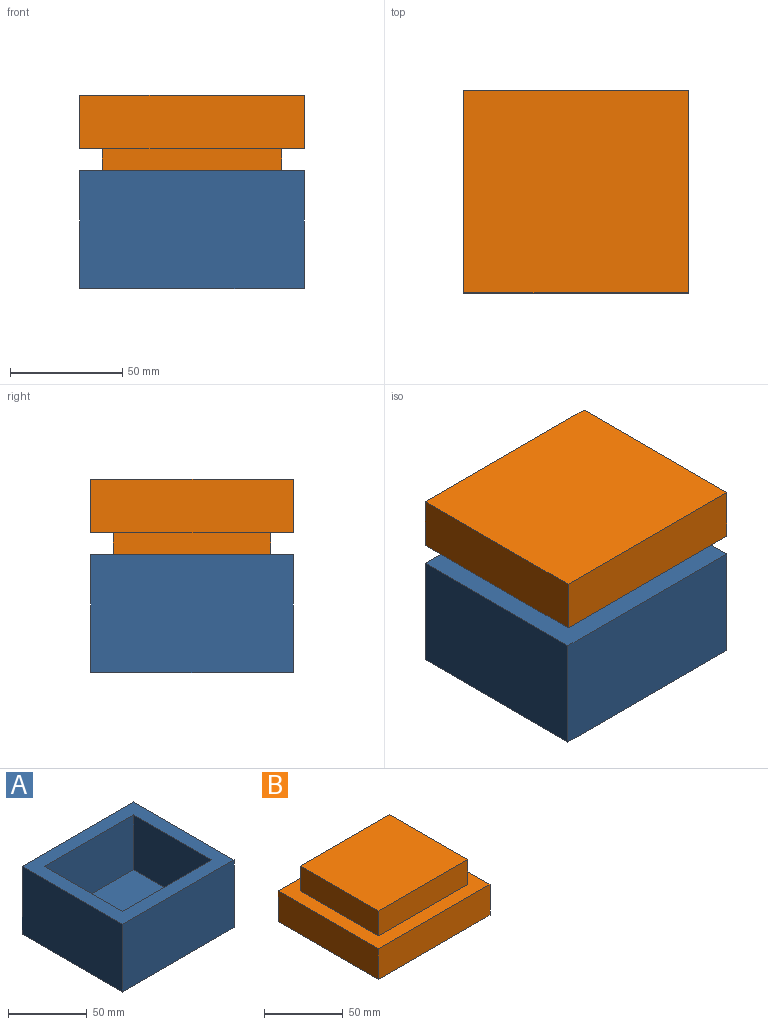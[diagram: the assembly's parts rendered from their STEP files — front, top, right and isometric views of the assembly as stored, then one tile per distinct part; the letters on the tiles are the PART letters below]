
ASSEMBLY  parts=2 mates=1
PART A: 11 faces, bbox 100x90x52.5 mm
  f0: plane 100x90mm, normal (0,0,1), area 3400mm2, adj f1,f2,f3,f4,f6,f7,f8,f9
  f1: plane 100x52.5mm, normal (0,1,0), area 5250mm2, adj f0,f2,f4,f5
  f2: plane 90x52.5mm, normal (-1,0,0), area 4725mm2, adj f0,f1,f3,f5
  f3: plane 100x52.5mm, normal (0,-1,0), area 5250mm2, adj f0,f2,f4,f5
  f4: plane 90x52.5mm, normal (1,0,0), area 4725mm2, adj f0,f1,f3,f5
  f5: plane 100x90mm, normal (0,0,-1), area 9000mm2, adj f1,f2,f3,f4
  f6: plane 80x42.5mm, normal (0,-1,0), area 3400mm2, adj f0,f7,f9,f10
  f7: plane 70x42.5mm, normal (1,0,0), area 2975mm2, adj f0,f6,f8,f10
  f8: plane 80x42.5mm, normal (0,1,0), area 3400mm2, adj f0,f7,f9,f10
  f9: plane 70x42.5mm, normal (-1,0,0), area 2975mm2, adj f0,f6,f8,f10
  f10: plane 80x70mm, normal (0,0,1), area 5600mm2, adj f6,f7,f8,f9
PART B: 11 faces, bbox 100x90x43.1 mm
  f0: plane 100x23.8mm, normal (0,1,0), area 2380mm2, adj f1,f3,f4,f5
  f1: plane 90x23.8mm, normal (-1,0,0), area 2142mm2, adj f0,f2,f4,f5
  f2: plane 100x23.8mm, normal (0,-1,0), area 2380mm2, adj f1,f3,f4,f5
  f3: plane 90x23.8mm, normal (1,0,0), area 2142mm2, adj f0,f2,f4,f5
  f4: plane 100x90mm, normal (0,0,1), area 3400mm2, adj f0,f1,f2,f3,f6,f7,f8,f9
  f5: plane 100x90mm, normal (0,0,-1), area 9000mm2, adj f0,f1,f2,f3
  f6: plane 70x19.3mm, normal (1,0,0), area 1351mm2, adj f4,f7,f9,f10
  f7: plane 80x19.3mm, normal (0,1,0), area 1544mm2, adj f4,f6,f8,f10
  f8: plane 70x19.3mm, normal (-1,0,0), area 1351mm2, adj f4,f7,f9,f10
  f9: plane 80x19.3mm, normal (0,-1,0), area 1544mm2, adj f4,f6,f8,f10
  f10: plane 80x70mm, normal (0,0,1), area 5600mm2, adj f6,f7,f8,f9
PLACE A t=(1.48,-93.48,21.14)mm
PLACE B rot(axis=(-1,0,0),180deg) t=(5.28,-98.96,107.09)mm
MATE slider A.f9 <-> B.f6  axis (-1,0,0) through (45.17,-98.96,73.64)mm
